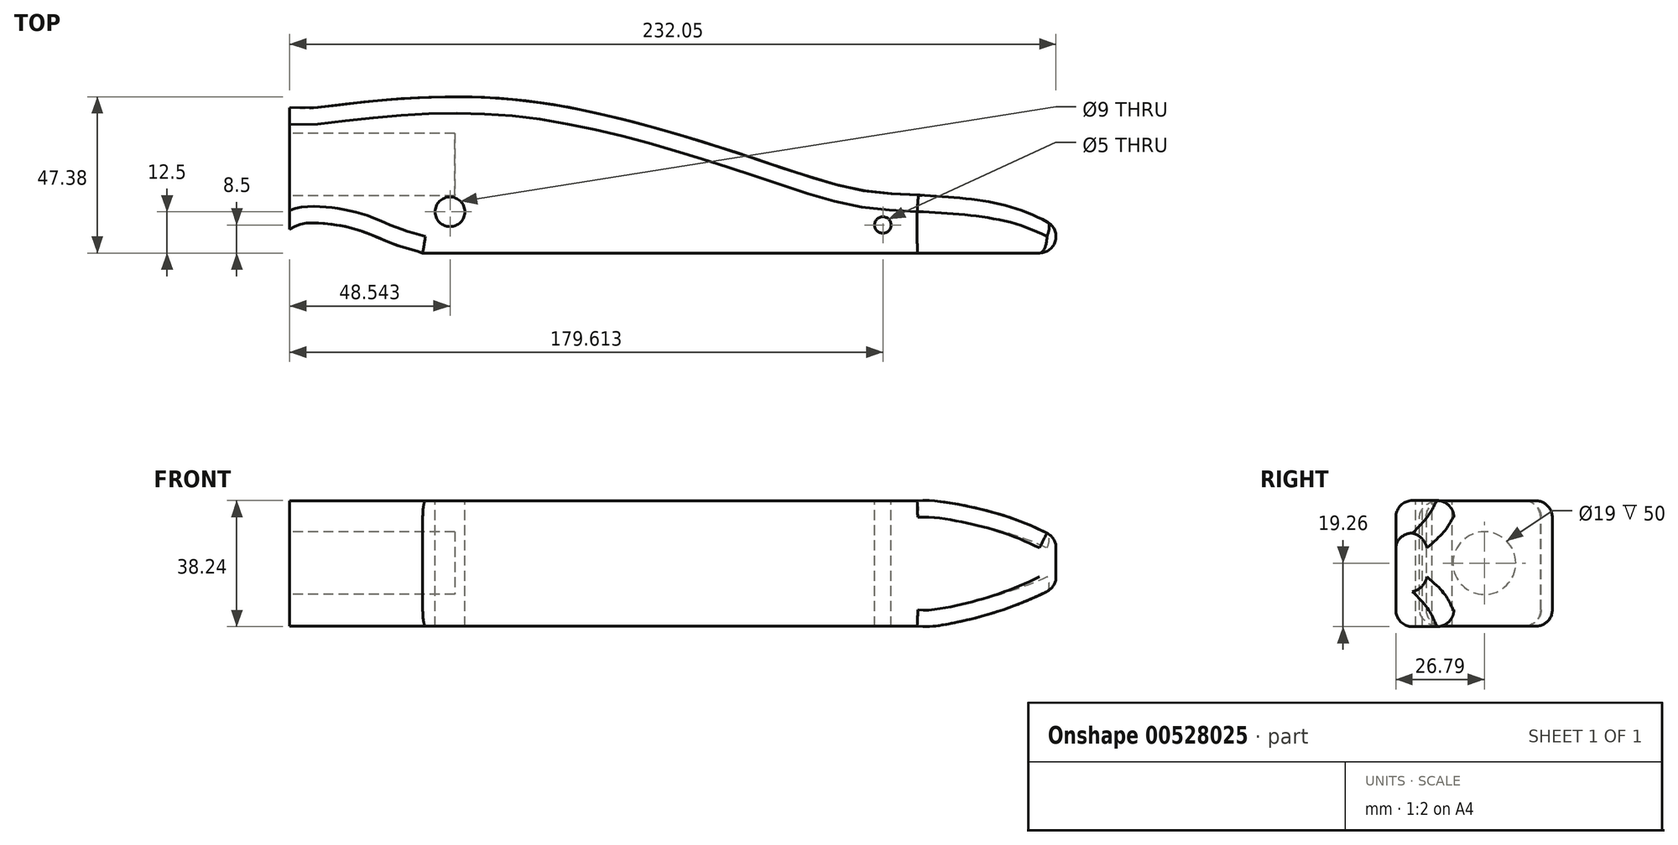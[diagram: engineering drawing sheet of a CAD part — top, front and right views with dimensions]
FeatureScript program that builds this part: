
annotation { "Feature Type Name" : "Feature", "Feature Type Description" : "" }
export const myFeature = defineFeature(function(context is Context, id is Id, definition is map)
    precondition{}
    {
        {
            var Q0;
            Q0=qCreatedBy(makeId("Top.planeOp"),FACE);
            var sketch = newSketch(context, id + "F0", { "sketchPlane" : qUnion([Q0])});
            skLineSegment(sketch, "E0.bottom", {"start": v(151.5, 36.5) * mm, "end": v(-151.5, 36.5) * mm});
            skLineSegment(sketch, "E0.top", {"start": v(151.5, -36.5) * mm, "end": v(-151.5, -36.5) * mm});
            skLineSegment(sketch, "E0.left", {"start": v(151.5, 36.5) * mm, "end": v(151.5, -36.5) * mm});
            skLineSegment(sketch, "E0.right", {"start": v(-151.5, 36.5) * mm, "end": v(-151.5, -36.5) * mm});
            skPoint(sketch, "E0.middle", {"position": v(0, 0) * mm});
            skSolve(sketch);
        }
        {
            var Q0;
            Q0=makeQuery(id+"F0.imprint","IMPRINT",FACE,{"disambiguationData":[TD([[makeQuery(id+"F0.imprint","IMPRINT",EDGE,{"derivedFrom":sQuery(id+"F0.wireOp",EDGE,"E0.bottom")}),1.0]])]});
            extrude(context, id + "F1", {"entities" : qUnion([Q0]), "depth" : 36.5 * mm, "hasSecondDirection" : true, "secondDirectionOppositeDirection" : true, "secondDirectionDepth" : 36.5 * mm});
        }
        {
            var Q0;
            Q0=makeQuery(id+"F1.opExtrude","SWEPT_FACE",FACE,{"disambiguationData":[OSD([sQuery(id+"F0.wireOp",EDGE,"E0.right")])]});
            var sketch = newSketch(context, id + "F2", { "sketchPlane" : qUnion([Q0])});
            skCircle(sketch, "E1", {"center": v(-4.75, 0) * mm, "radius": 9.5 * mm});
            skSolve(sketch);
        }
        {
            var Q0;
            Q0=makeQuery(id+"F2.imprint","IMPRINT",FACE,{"disambiguationData":[TD([[makeQuery(id+"F2.imprint","IMPRINT",EDGE,{"derivedFrom":sQuery(id+"F2.wireOp",EDGE,"E1")}),1.0]])]});
            var Q1;
            Q1=sQuery(id+"F2.wireOp",EDGE,"E1");
            extrude(context, id + "F3", {"entities" : qUnion([Q0]), "operationType" : NewBodyOperationType.REMOVE, "surfaceEntities" : qUnion([Q1]), "oppositeDirection" : true, "depth" : 50 * mm});
        }
        {
            var Q0;
            Q0=makeQuery(id+"F1.opExtrude","SWEPT_FACE",FACE,{"disambiguationData":[OSD([sQuery(id+"F0.wireOp",EDGE,"E0.bottom")])]});
            var sketch = newSketch(context, id + "F4", { "sketchPlane" : qUnion([Q0])});
            skLineSegment(sketch, "E2", {"start": v(151.5, -19.13) * mm, "end": v(-38.5, -19.13) * mm});
            skLineSegment(sketch, "E3", {"start": v(151.5, -19.13) * mm, "end": v(151.5, 18.87) * mm});
            skLineSegment(sketch, "E4", {"start": v(151.5, 18.87) * mm, "end": v(-38.5, 18.87) * mm});
            skPoint(sketch, "E5", {"position": v(-93.5, 0) * mm});
            skFitSpline(sketch, "E6", {"points": [v(-38.5, -19.13) * mm, v(-43.44, -19.13) * mm, v(-67.69, -13) * mm, v(-93.5, 0) * mm], "startDerivative": vector(-22.41, -1.99) * mm, "endDerivative": vector(-57.1, 33.17) * mm});
            skFitSpline(sketch, "E7", {"points": [v(-38.5, 18.87) * mm, v(-43.28, 18.87) * mm, v(-67.7, 13.43) * mm, v(-93.5, 0) * mm], "startDerivative": vector(-21.83, 1.57) * mm, "endDerivative": vector(-56.5, -34.97) * mm});
            skSolve(sketch);
        }
        {
            var Q0;
            Q0=makeQuery(id+"F1.opExtrude","CAP_FACE",FACE,{"disambiguationData":[OSD([sQuery(id+"F0.wireOp",EDGE,"E0.bottom"),sQuery(id+"F0.wireOp",EDGE,"E0.top"),sQuery(id+"F0.wireOp",EDGE,"E0.left"),sQuery(id+"F0.wireOp",EDGE,"E0.right")])],"isStart":false});
            var sketch = newSketch(context, id + "F5", { "sketchPlane" : qUnion([Q0])});
            skFitSpline(sketch, "E8", {"points": [v(-151.5, 21.96) * mm, v(-144.34, 21.96) * mm, v(-81.76, 24.32) * mm, v(9.35, 0) * mm, v(31.26, -4.04) * mm, v(64.85, -7.5) * mm, v(93.5, -22.04) * mm], "startDerivative": vector(72.07, -8.85) * mm, "endDerivative": vector(230.66, -143.14) * mm});
            skPoint(sketch, "E9", {"position": v(-95.5, -14.04) * mm});
            skPoint(sketch, "E10", {"position": v(44.5, -14.04) * mm});
            skLineSegment(sketch, "E11", {"start": v(93.5, -22.04) * mm, "end": v(-111.22, -22.04) * mm});
            skFitSpline(sketch, "E12", {"points": [v(-111.22, -22.04) * mm, v(-119.63, -19.46) * mm, v(-129.96, -15.3) * mm, v(-141.72, -13) * mm, v(-151.5, -14.87) * mm], "startDerivative": vector(-36.54, 12.42) * mm, "endDerivative": vector(-32.07, -25.43) * mm});
            skLineSegment(sketch, "E13", {"start": v(-151.5, 21.96) * mm, "end": v(-151.5, -14.87) * mm});
            skCircle(sketch, "E14", {"center": v(-95.5, -14.04) * mm, "radius": 3.15 * mm});
            skCircle(sketch, "E15", {"center": v(44.5, -14.04) * mm, "radius": 2.94 * mm});
            skSolve(sketch);
        }
        {
            var Q0;
            {var subQ1=sQuery(id+"F4.wireOp",EDGE,"E2");Q0=makeQuery(id+"F4.imprint","IMPRINT",FACE,{"disambiguationData":[TD([[makeQuery(id+"F4.imprint","IMPRINT",EDGE,{"derivedFrom":subQ1}),1.0]])]});}
            extrude(context, id + "F6", {"entities" : qUnion([Q0]), "operationType" : NewBodyOperationType.REMOVE, "endBound" : BoundingType.THROUGH_ALL, "oppositeDirection" : true, "depth" : 25 * mm, "offsetDistance" : 25 * mm});
        }
        {
            var Q0;
            {var subQ2=sQuery(id+"F5.wireOp",EDGE,"E8");Q0=makeQuery(id+"F5.imprint","IMPRINT",FACE,{"disambiguationData":[TD([[makeQuery(id+"F5.imprint","IMPRINT",EDGE,{"derivedFrom":subQ2}),1.0]])]});}
            extrude(context, id + "F7", {"entities" : qUnion([Q0]), "operationType" : NewBodyOperationType.REMOVE, "endBound" : BoundingType.THROUGH_ALL, "oppositeDirection" : true, "depth" : 25 * mm, "offsetDistance" : 25 * mm});
        }
        {
            var Q0;
            Q0=makeQuery(id+"F7.boolean.opBoolean","INTERSECT",EDGE,{"derivedFrom":[makeQuery(id+"F6.boolean.opBoolean","COPY",FACE,{"derivedFrom":makeQuery(id+"F6.opExtrude","SWEPT_FACE",FACE,{"disambiguationData":[OSD([sQuery(id+"F4.wireOp",EDGE,"E4")])]})}),makeQuery(id+"F7.opExtrude","SWEPT_FACE",FACE,{"disambiguationData":[OSD([sQuery(id+"F5.wireOp",EDGE,"E12")])]})]});
            var Q1;
            Q1=makeQuery(id+"F7.boolean.opBoolean","INTERSECT",EDGE,{"derivedFrom":[makeQuery(id+"F6.boolean.opBoolean","COPY",FACE,{"derivedFrom":makeQuery(id+"F6.opExtrude","SWEPT_FACE",FACE,{"disambiguationData":[OSD([sQuery(id+"F4.wireOp",EDGE,"E4")])]})}),makeQuery(id+"F7.opExtrude","SWEPT_FACE",FACE,{"disambiguationData":[OSD([sQuery(id+"F5.wireOp",EDGE,"E11")])]})]});
            var Q2;
            Q2=makeQuery(id+"F7.boolean.opBoolean","INTERSECT",EDGE,{"derivedFrom":[makeQuery(id+"F6.boolean.opBoolean","COPY",FACE,{"derivedFrom":makeQuery(id+"F6.opExtrude","SWEPT_FACE",FACE,{"disambiguationData":[OSD([sQuery(id+"F4.wireOp",EDGE,"E4")])]})}),makeQuery(id+"F7.opExtrude","SWEPT_FACE",FACE,{"disambiguationData":[OSD([sQuery(id+"F5.wireOp",EDGE,"E8")])]})]});
            var Q3;
            Q3=makeQuery(id+"F6.boolean.opBoolean","COPY",EDGE,{"derivedFrom":makeQuery(id+"F6.opExtrude","SWEPT_EDGE",EDGE,{"disambiguationData":[OSD([sQuery(id+"F0.wireOp",EDGE,"E0.bottom"),sQuery(id+"F0.wireOp",EDGE,"E0.right"),sQuery(id+"F4.wireOp",EDGE,"E3"),sQuery(id+"F4.wireOp",EDGE,"E4")])]})});
            var Q4;
            Q4=makeQuery(id+"F7.boolean.opBoolean","COPY",EDGE,{"derivedFrom":makeQuery(id+"F7.opExtrude","SWEPT_EDGE",EDGE,{"disambiguationData":[OSD([sQuery(id+"F0.wireOp",EDGE,"E0.right"),sQuery(id+"F5.wireOp",EDGE,"E8"),sQuery(id+"F5.wireOp",EDGE,"E13")])]})});
            var Q5;
            Q5=makeQuery(id+"F7.boolean.opBoolean","COPY",EDGE,{"derivedFrom":makeQuery(id+"F7.opExtrude","SWEPT_EDGE",EDGE,{"disambiguationData":[OSD([sQuery(id+"F0.wireOp",EDGE,"E0.right"),sQuery(id+"F5.wireOp",EDGE,"E12"),sQuery(id+"F5.wireOp",EDGE,"E13")])]})});
            var Q6;
            Q6=makeQuery(id+"F6.boolean.opBoolean","COPY",EDGE,{"derivedFrom":makeQuery(id+"F6.opExtrude","SWEPT_EDGE",EDGE,{"disambiguationData":[OSD([sQuery(id+"F0.wireOp",EDGE,"E0.bottom"),sQuery(id+"F0.wireOp",EDGE,"E0.right"),sQuery(id+"F4.wireOp",EDGE,"E2"),sQuery(id+"F4.wireOp",EDGE,"E3")])]})});
            var Q7;
            Q7=makeQuery(id+"F7.boolean.opBoolean","INTERSECT",EDGE,{"derivedFrom":[makeQuery(id+"F6.boolean.opBoolean","COPY",FACE,{"derivedFrom":makeQuery(id+"F6.opExtrude","SWEPT_FACE",FACE,{"disambiguationData":[OSD([sQuery(id+"F4.wireOp",EDGE,"E2")])]})}),makeQuery(id+"F7.opExtrude","SWEPT_FACE",FACE,{"disambiguationData":[OSD([sQuery(id+"F5.wireOp",EDGE,"E8")])]})]});
            var Q8;
            Q8=makeQuery(id+"F7.boolean.opBoolean","INTERSECT",EDGE,{"derivedFrom":[makeQuery(id+"F6.boolean.opBoolean","COPY",FACE,{"derivedFrom":makeQuery(id+"F6.opExtrude","SWEPT_FACE",FACE,{"disambiguationData":[OSD([sQuery(id+"F4.wireOp",EDGE,"E2")])]})}),makeQuery(id+"F7.opExtrude","SWEPT_FACE",FACE,{"disambiguationData":[OSD([sQuery(id+"F5.wireOp",EDGE,"E11")])]})]});
            var Q9;
            Q9=makeQuery(id+"F7.boolean.opBoolean","INTERSECT",EDGE,{"derivedFrom":[makeQuery(id+"F6.boolean.opBoolean","COPY",FACE,{"derivedFrom":makeQuery(id+"F6.opExtrude","SWEPT_FACE",FACE,{"disambiguationData":[OSD([sQuery(id+"F4.wireOp",EDGE,"E2")])]})}),makeQuery(id+"F7.opExtrude","SWEPT_FACE",FACE,{"disambiguationData":[OSD([sQuery(id+"F5.wireOp",EDGE,"E12")])]})]});
            fillet(context, id + "F8", {"entities" : qUnion([Q0, Q1, Q2, Q3, Q4, Q5, Q6, Q7, Q8, Q9]), "radius" : 5 * mm, "tangentPropagation" : true, "allowEdgeOverflow" : false});
        }
        {
            var Q0;
            Q0=makeQuery(id+"F7.boolean.opBoolean","INTERSECT",EDGE,{"derivedFrom":[makeQuery(id+"F6.boolean.opBoolean","COPY",FACE,{"derivedFrom":makeQuery(id+"F6.opExtrude","SWEPT_FACE",FACE,{"disambiguationData":[OSD([sQuery(id+"F4.wireOp",EDGE,"E6")])]})}),makeQuery(id+"F7.opExtrude","SWEPT_FACE",FACE,{"disambiguationData":[OSD([sQuery(id+"F5.wireOp",EDGE,"E8")])]})]});
            var Q1;
            Q1=makeQuery(id+"F7.boolean.opBoolean","INTERSECT",EDGE,{"derivedFrom":[makeQuery(id+"F6.boolean.opBoolean","COPY",FACE,{"derivedFrom":makeQuery(id+"F6.opExtrude","SWEPT_FACE",FACE,{"disambiguationData":[OSD([sQuery(id+"F4.wireOp",EDGE,"E6")])]})}),makeQuery(id+"F7.opExtrude","SWEPT_FACE",FACE,{"disambiguationData":[OSD([sQuery(id+"F5.wireOp",EDGE,"E11")])]})]});
            var Q2;
            Q2=makeQuery(id+"F7.boolean.opBoolean","INTERSECT",EDGE,{"derivedFrom":[makeQuery(id+"F6.boolean.opBoolean","COPY",FACE,{"derivedFrom":makeQuery(id+"F6.opExtrude","SWEPT_FACE",FACE,{"disambiguationData":[OSD([sQuery(id+"F4.wireOp",EDGE,"E7")])]})}),makeQuery(id+"F7.opExtrude","SWEPT_FACE",FACE,{"disambiguationData":[OSD([sQuery(id+"F5.wireOp",EDGE,"E8")])]})]});
            var Q3;
            Q3=makeQuery(id+"F7.boolean.opBoolean","INTERSECT",EDGE,{"derivedFrom":[makeQuery(id+"F6.boolean.opBoolean","COPY",FACE,{"derivedFrom":makeQuery(id+"F6.opExtrude","SWEPT_FACE",FACE,{"disambiguationData":[OSD([sQuery(id+"F4.wireOp",EDGE,"E7")])]})}),makeQuery(id+"F7.opExtrude","SWEPT_FACE",FACE,{"disambiguationData":[OSD([sQuery(id+"F5.wireOp",EDGE,"E11")])]})]});
            fillet(context, id + "F9", {"entities" : qUnion([Q0, Q1, Q2, Q3]), "radius" : 5 * mm, "tangentPropagation" : true, "allowEdgeOverflow" : false});
        }
        {
            var Q0;
            Q0=makeQuery(id+"F6.boolean.opBoolean","COPY",FACE,{"derivedFrom":makeQuery(id+"F6.opExtrude","SWEPT_FACE",FACE,{"disambiguationData":[OSD([sQuery(id+"F4.wireOp",EDGE,"E4")])]})});
            var sketch = newSketch(context, id + "F10", { "sketchPlane" : qUnion([Q0])});
            skCircle(sketch, "E16", {"center": v(-102.96, -9.54) * mm, "radius": 4.5 * mm});
            skCircle(sketch, "E17", {"center": v(29.12, -13.54) * mm, "radius": 2.5 * mm});
            skSolve(sketch);
        }
        {
            var Q0;
            Q0=makeQuery(id+"F10.imprint","IMPRINT",FACE,{"disambiguationData":[TD([[makeQuery(id+"F10.imprint","IMPRINT",EDGE,{"derivedFrom":sQuery(id+"F10.wireOp",EDGE,"E16")}),1.0]])]});
            var Q1;
            Q1=sQuery(id+"F10.wireOp",EDGE,"E16");
            extrude(context, id + "F11", {"entities" : qUnion([Q0]), "operationType" : NewBodyOperationType.REMOVE, "surfaceEntities" : qUnion([Q1]), "endBound" : BoundingType.THROUGH_ALL, "oppositeDirection" : true, "depth" : 25 * mm, "offsetDistance" : 25 * mm});
        }
        {
            var Q0;
            Q0=makeQuery(id+"F6.boolean.opBoolean","COPY",FACE,{"derivedFrom":makeQuery(id+"F6.opExtrude","SWEPT_FACE",FACE,{"disambiguationData":[OSD([sQuery(id+"F4.wireOp",EDGE,"E4")])]})});
            var sketch = newSketch(context, id + "F12", { "sketchPlane" : qUnion([Q0])});
            skCircle(sketch, "E18", {"center": v(28.11, -13.54) * mm, "radius": 2.5 * mm});
            skSolve(sketch);
        }
        {
            var Q0;
            Q0=makeQuery(id+"F12.imprint","IMPRINT",FACE,{"disambiguationData":[TD([[makeQuery(id+"F12.imprint","IMPRINT",EDGE,{"derivedFrom":sQuery(id+"F12.wireOp",EDGE,"E18")}),1.0]])]});
            extrude(context, id + "F13", {"entities" : qUnion([Q0]), "operationType" : NewBodyOperationType.REMOVE, "endBound" : BoundingType.THROUGH_ALL, "oppositeDirection" : true, "depth" : 25 * mm, "offsetDistance" : 25 * mm});
        }
    });
